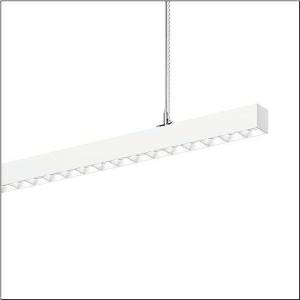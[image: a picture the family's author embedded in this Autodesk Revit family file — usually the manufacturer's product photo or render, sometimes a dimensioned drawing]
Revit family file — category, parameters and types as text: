
# Revit family: silica_r__21_51mx36da47wb_ab97
name_source: partatom
category: Lighting Fixtures
units: mm (PartAtom-declared; Revit-internal decimal feet)

## family parameters
Cut with Voids When Loaded = No
Host = Face
Light Source = No
Part Type = Normal
Room Calculation Point = No
Round Connector Dimension = Use Diameter
Shared = No

## types (1)
- --- (1 x LED, 7060 lm, 40.3 W, 4000K)
    Apparent Load = 40 VA
    CIE Flux Codes = 83 98 100 61 100
    Color Rendering = 80
    Color Temperature = 4000K
    Default Elevation = 1800 mm
    Description = Silica® 21, office luminaire, primary light control with darklight reflector, of PMMA, white, CAT 2 (L<= 3000cd/m²), light emission: direct/indirect distribution, primary light characteristic: symmetric, installation type: suspended mounting, LED, rated luminous flux: 7.060lm, luminous efficacy: 175lm/W, light colour: 840, colour temperature: 4000K, control gear: DALI 2, with terminal, 3+2-pole, max. 2.5mm², mains connection: 220..240V, AC, 50/60Hz, rated input power: 40.3W, luminaire housing, of aluminium, traffic white (RAL 9016), length: 1.204mm, width: 53mm, height: 53mm, protection rating (complete): IP20, insulation class (complete): insulation class I (protective earthing), certification: CE, permissible operating ambient temperature: 0..+35°C, standard: EN 50419, packaging unit: 1 piece
    Height = 53 mm
    Lamp = 1 x LED
    Lamp Light Flux = 7060 lm
    Lamp Power = 40.3 W
    Lamp count = 1
    Length = 1204 mm
    Luminous efficacy = 175 lm/W
    Manufacturer = Siteco
    ModVariant = No
    Model = 51MX36DA47WB
    Mounting Place = Ceiling
    Mounting Type = Pendant
    Number of Poles = 1
    OnlyDefault = Yes
    Power Factor = 1
    Product Name = Silica® 21
    Product group = office luminaire | ceiling pendant
    ProductGroupID = 904
    Protection Class = Protection class I
    Protection Degree = IP 20
    RLX_Detail_Level = 1
    RLX_Emergency_Light_Flux = 0 lm
    RLX_Emergency_Type = 0
    RLX_Emergency_Type_DB = No
    RlxData = <blob elided: 40961 chars, md5=20a7041e>
    Socket = socket
    Standby Power = 0 W
    System Light Flux = 7060 lm
    System Power = 40 W
    Type Comments = factory setting: luminous flux: 100 % | dim-lin: 254 | 336 mA
    Type Image = l_1335921.jpg
    URL = http://relux.com
    VarID = @adj_121396
    Voltage = 0 V
    Weight = 0.00 kg
    Width = 53 mm

## geometry (parser evidence)
native form markers: Blend x4, Sweep x12
no freeform markers — native parametric forms only
